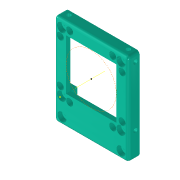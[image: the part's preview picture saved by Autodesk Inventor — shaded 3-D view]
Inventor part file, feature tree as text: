
AUTODESK INVENTOR PART (.ipt)
format: ipt  version: 2022 (Build 260153000, 153)  size: 386,048 bytes
history: native  units: mm
features: other x13, reference x12, sketch x6, hole x5, plane x3, extrude x2, fillet x1, chamfer x1, projected_geometry x1
ambient origin geometry x8: Origin, YZ Plane, XZ Plane, XY Plane, X Axis, Y Axis, Z Axis, Center Point
bodies: Solid1 (feature_tree)
feature tree (44):
  plane  "Work Plane1"
  extrude  "Extrusion1"  Depth=2.0mm
  fillet  "Fillet1"  Radius=49.8mm
  other  "Work Axis2"
  hole  "Hole2"  [1 undecoded]
  chamfer  "Chamfer2"  Distance=2.5mm
  hole  "Hole3"  [1 undecoded]
  hole  "Hole4"  [1 undecoded]
  hole  "Hole5"  [1 undecoded]
  extrude  "Extrusion3"  Depth=10.0mm
  plane  "Work Plane2"
  plane  "Work Plane3"
  hole  "Hole6"  [1 undecoded]
  sketch  "Sketch1"  dims[d0=7.7mm d1=0.0mm d2=2.0mm]
  reference  "Reference1"
  other  "Work Axis1"
  sketch  "Sketch4"  dims[d20=3.2mm d21=6.0mm d22=6.0mm d23=3.1mm d24=90.0deg d25=12.0mm d26=20.594885mm]
  sketch  "Sketch6"  dims[d27=4.6mm d28=2.0mm d29=45.0deg d34=49.8mm]
  sketch  "Sketch7"  dims[d35=49.8mm d36=5.5mm]
  sketch  "Sketch9"  dims[d37=2.5mm]
  reference  "Reference7"
  sketch  "Sketch14"  dims[d38=2.5mm d39=2.5mm d40=2.5mm d41=2.5mm d42=2.5mm d43=2.5mm d44=2.5mm d45=2.0mm d46=5.0mm d47=5.0mm d48=5.0mm d49=5.0mm d51=5.0mm d52=0.5mm d53=5.0mm d54=5.0mm d55=2.8mm d56=2.8mm d57=2.8mm d58=2.8mm d63=2.8mm d64=2.8mm d65=4.9mm d66=4.9mm d67=4.9mm d68=4.9mm d69=2.8mm d70=6.0mm d71=4.0mm d72=2.0mm d73=90.0deg d74=6.5mm d75=20.594885mm d76=2.8mm d77=6.0mm d78=4.0mm d79=2.0mm d80=90.0deg d81=6.5mm d82=20.594885mm d83=2.8mm d84=6.0mm d85=4.0mm d86=2.0mm d87=90.0deg d88=6.5mm d89=20.594885mm d90=7.85mm d91=135.0deg d92=135.0deg d93=10.0mm d94=0.0mm d105=4.7mm d106=6.0mm d107=4.0mm d108=2.0mm d109=90.0deg d110=8.0mm d111=20.594885mm]
  projected_geometry  "Projected Loop4"
  reference  "Reference9"
  reference  "Reference10"
  reference  "Reference11"
  reference  "Reference12"
  reference  "Reference13"
  reference  "Reference14"
  reference  "Reference15"
  reference  "Reference16"
  reference  "Referenz17"
  reference  "Referenz18"
  other  "<userpath>\Dropbox\UC2\02_CAD\INVENTOR\uc2_v3\Assembly_Cube_explosion_1x1_v3.iam"
  other  "Assembly_Cube_explosion_1x1_v3.iam"
  other  "10_Cube_1x1_v3:1"
  other  "Assembly_Cube_empty_1x1_v2.iam"
  other  "10_Base_v2_puzzle:2"
  other  "Assembly_Cube_Dichroic_Beamsplitter_multi_motorized_25x35_linearmotor_90degreerot_v3.iam"
  other  "20_Cube_Insert_Beamsplittercube_motorized_cube_base:1"
  other  "Assembly_Cube_empty_1x1_v2_IM.iam"
  other  "10_Cube_1x1_v2_IM:1"
  other  "Assembly_Cube_v2.iam"
  other  "10_Cube_Base:1"
note: 5 required parameter values undecoded (feature->parameter linkage not recoverable at this tier; creation-order binding heuristic only, values carry confidence <= 0.55)
